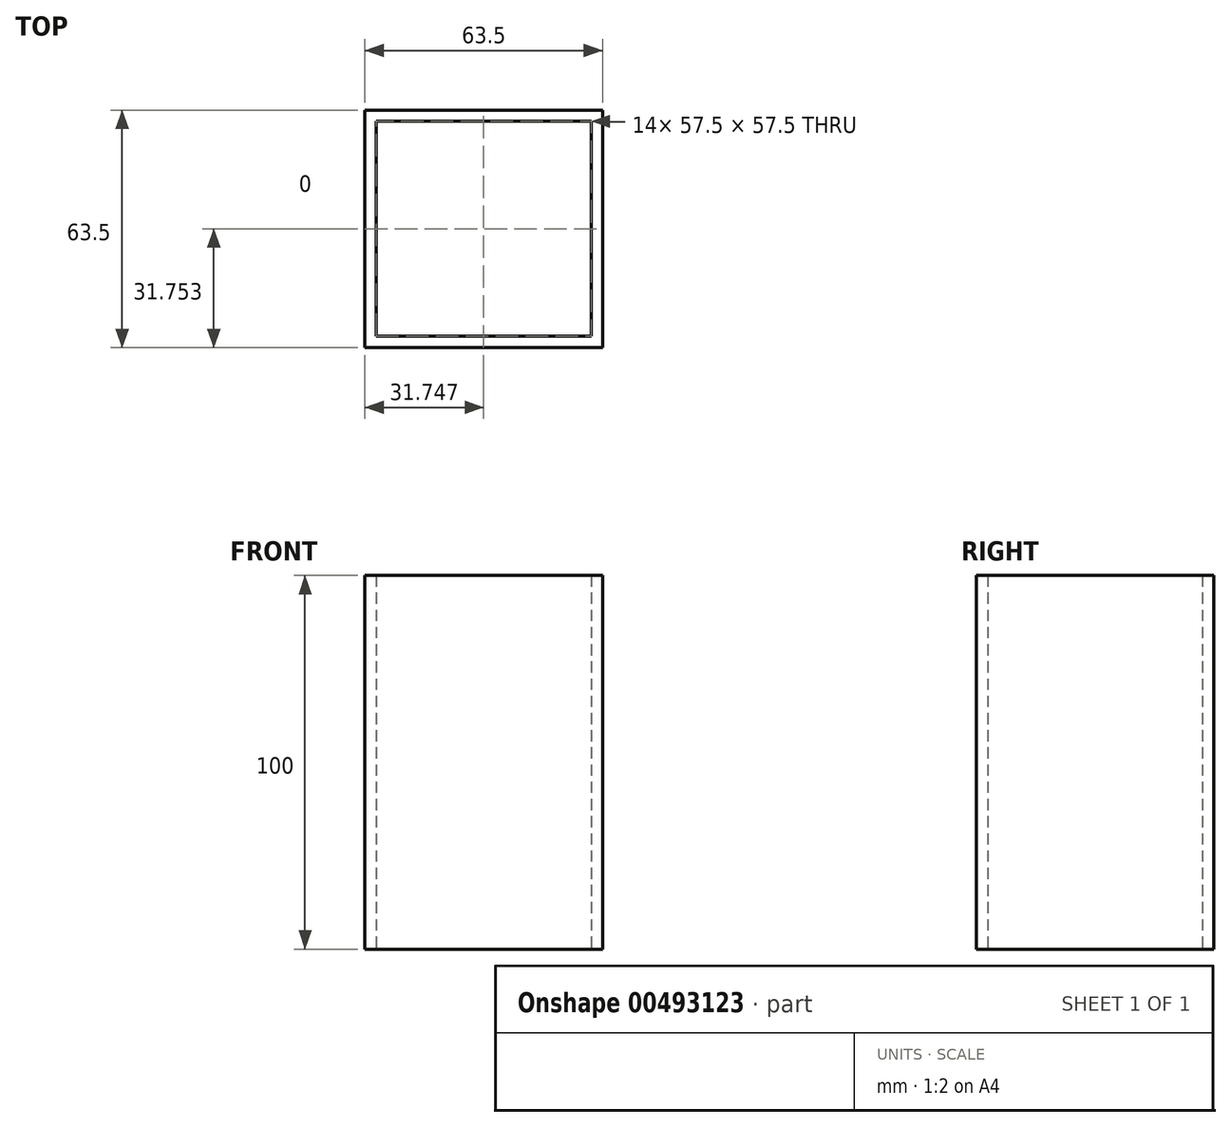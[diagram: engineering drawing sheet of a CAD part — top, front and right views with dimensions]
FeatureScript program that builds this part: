
annotation { "Feature Type Name" : "Feature", "Feature Type Description" : "" }
export const myFeature = defineFeature(function(context is Context, id is Id, definition is map)
    precondition{}
    {
        {
            var Q0;
            Q0=qCreatedBy(makeId("Top.planeOp"),FACE);
            var sketch = newSketch(context, id + "F0", { "sketchPlane" : qUnion([Q0])});
            skLineSegment(sketch, "E0.bottom", {"start": v(-27.63, 16.07) * mm, "end": v(29.87, 16.07) * mm});
            skLineSegment(sketch, "E0.top", {"start": v(-27.63, -41.43) * mm, "end": v(29.87, -41.43) * mm});
            skLineSegment(sketch, "E0.left", {"start": v(-27.63, 16.07) * mm, "end": v(-27.63, -41.43) * mm});
            skLineSegment(sketch, "E0.right", {"start": v(29.87, 16.07) * mm, "end": v(29.87, -41.43) * mm});
            skLineSegment(sketch, "E1.bottom", {"start": v(-30.63, 19.07) * mm, "end": v(32.87, 19.07) * mm});
            skLineSegment(sketch, "E1.top", {"start": v(-30.63, -44.43) * mm, "end": v(32.87, -44.43) * mm});
            skLineSegment(sketch, "E1.left", {"start": v(-30.63, 19.07) * mm, "end": v(-30.63, -44.43) * mm});
            skLineSegment(sketch, "E1.right", {"start": v(32.87, 19.07) * mm, "end": v(32.87, -44.43) * mm});
            skSolve(sketch);
        }
        {
            var Q0;
            Q0 = qSketchRegion(id + "F0", true);
            extrude(context, id + "F1", {"entities" : qUnion([Q0]), "depth" : 100 * mm});
        }
    });
